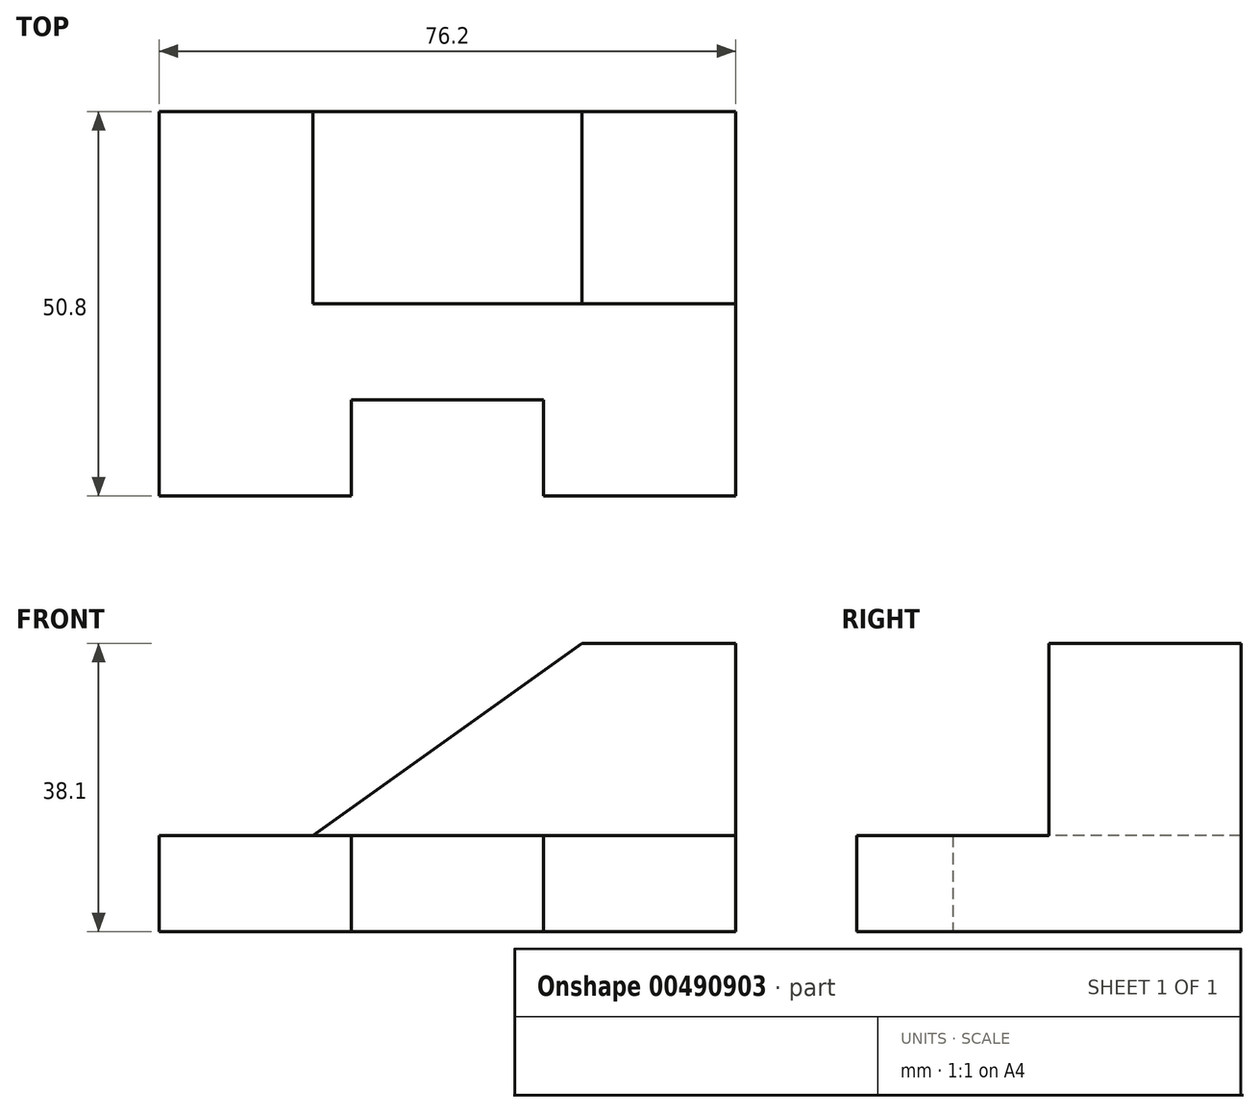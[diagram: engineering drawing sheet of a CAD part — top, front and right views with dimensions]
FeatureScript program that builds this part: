
annotation { "Feature Type Name" : "Feature", "Feature Type Description" : "" }
export const myFeature = defineFeature(function(context is Context, id is Id, definition is map)
    precondition{}
    {
        {
            var Q0;
            Q0=qCreatedBy(makeId("Top.planeOp"),FACE);
            var sketch = newSketch(context, id + "F0", { "sketchPlane" : qUnion([Q0])});
            skLineSegment(sketch, "E0", {"start": v(0, 0) * mm, "end": v(0, 50.8) * mm});
            skLineSegment(sketch, "E1", {"start": v(0, 50.8) * mm, "end": v(20.32, 50.8) * mm});
            skLineSegment(sketch, "E2", {"start": v(20.32, 50.8) * mm, "end": v(55.88, 50.8) * mm});
            skLineSegment(sketch, "E3", {"start": v(55.88, 50.8) * mm, "end": v(76.2, 50.8) * mm});
            skLineSegment(sketch, "E4", {"start": v(76.2, 50.8) * mm, "end": v(76.2, 25.4) * mm});
            skLineSegment(sketch, "E5", {"start": v(76.2, 25.4) * mm, "end": v(76.2, 0) * mm});
            skLineSegment(sketch, "E6", {"start": v(0, 0) * mm, "end": v(25.4, 0) * mm});
            skLineSegment(sketch, "E7", {"start": v(25.4, 0) * mm, "end": v(25.4, 12.7) * mm});
            skLineSegment(sketch, "E8", {"start": v(25.4, 12.7) * mm, "end": v(50.8, 12.7) * mm});
            skLineSegment(sketch, "E9", {"start": v(50.8, 12.7) * mm, "end": v(50.8, 0) * mm});
            skLineSegment(sketch, "E10", {"start": v(50.8, 0) * mm, "end": v(76.2, 0) * mm});
            skLineSegment(sketch, "E11", {"start": v(20.32, 50.8) * mm, "end": v(20.32, 25.4) * mm});
            skLineSegment(sketch, "E12", {"start": v(20.32, 25.4) * mm, "end": v(76.2, 25.4) * mm});
            skLineSegment(sketch, "E13", {"start": v(55.88, 50.8) * mm, "end": v(55.88, 25.4) * mm});
            skSolve(sketch);
        }
        {
            var Q0;
            Q0=makeQuery(id+"F0.imprint","IMPRINT",FACE,{"disambiguationData":[TD([[makeQuery(id+"F0.imprint","IMPRINT",EDGE,{"derivedFrom":sQuery(id+"F0.wireOp",EDGE,"E0")}),-1.0]])]});
            extrude(context, id + "F1", {"entities" : qUnion([Q0]), "depth" : 12.7 * mm});
        }
        {
            var Q0;
            Q0=makeQuery(id+"F0.imprint","IMPRINT",FACE,{"disambiguationData":[TD([[makeQuery(id+"F0.imprint","IMPRINT",EDGE,{"derivedFrom":sQuery(id+"F0.wireOp",EDGE,"E3")}),-1.0]])]});
            extrude(context, id + "F2", {"entities" : qUnion([Q0]), "operationType" : NewBodyOperationType.ADD, "depth" : 38.1 * mm});
        }
        {
            var Q0;
            Q0=makeQuery(id+"F0.imprint","IMPRINT",FACE,{"disambiguationData":[TD([[makeQuery(id+"F0.imprint","IMPRINT",EDGE,{"derivedFrom":sQuery(id+"F0.wireOp",EDGE,"E2")}),-1.0]])]});
            extrude(context, id + "F3", {"entities" : qUnion([Q0]), "operationType" : NewBodyOperationType.ADD, "depth" : 38.1 * mm});
        }
        {
            var Q0;
            {var subQ0=sQuery(id+"F0.wireOp",EDGE,"E12");Q0=makeQuery(id+"F3.boolean.opBoolean","MERGE",FACE,{"derivedFrom":[makeQuery(id+"F2.opExtrude","SWEPT_FACE",FACE,{"disambiguationData":[OSD([subQ0])]}),makeQuery(id+"F3.opExtrude","SWEPT_FACE",FACE,{"disambiguationData":[OSD([subQ0])]})]});}
            var sketch = newSketch(context, id + "F4", { "sketchPlane" : qUnion([Q0])});
            skLineSegment(sketch, "E14", {"start": v(20.32, 12.7) * mm, "end": v(55.88, 12.7) * mm});
            skLineSegment(sketch, "E15", {"start": v(55.88, 12.7) * mm, "end": v(55.88, 38.1) * mm});
            skLineSegment(sketch, "E16", {"start": v(55.88, 38.1) * mm, "end": v(20.32, 12.7) * mm});
            skSolve(sketch);
        }
        {
            var Q0;
            {var subQ0=sQuery(id+"F4.wireOp",EDGE,"E16");Q0=makeQuery(id+"F4.imprint","IMPRINT",FACE,{"disambiguationData":[TD([[makeQuery(id+"F4.imprint","IMPRINT",EDGE,{"derivedFrom":subQ0}),-1.0]])]});}
            extrude(context, id + "F5", {"entities" : qUnion([Q0]), "operationType" : NewBodyOperationType.REMOVE, "oppositeDirection" : true, "depth" : 25.4 * mm});
        }
    });
